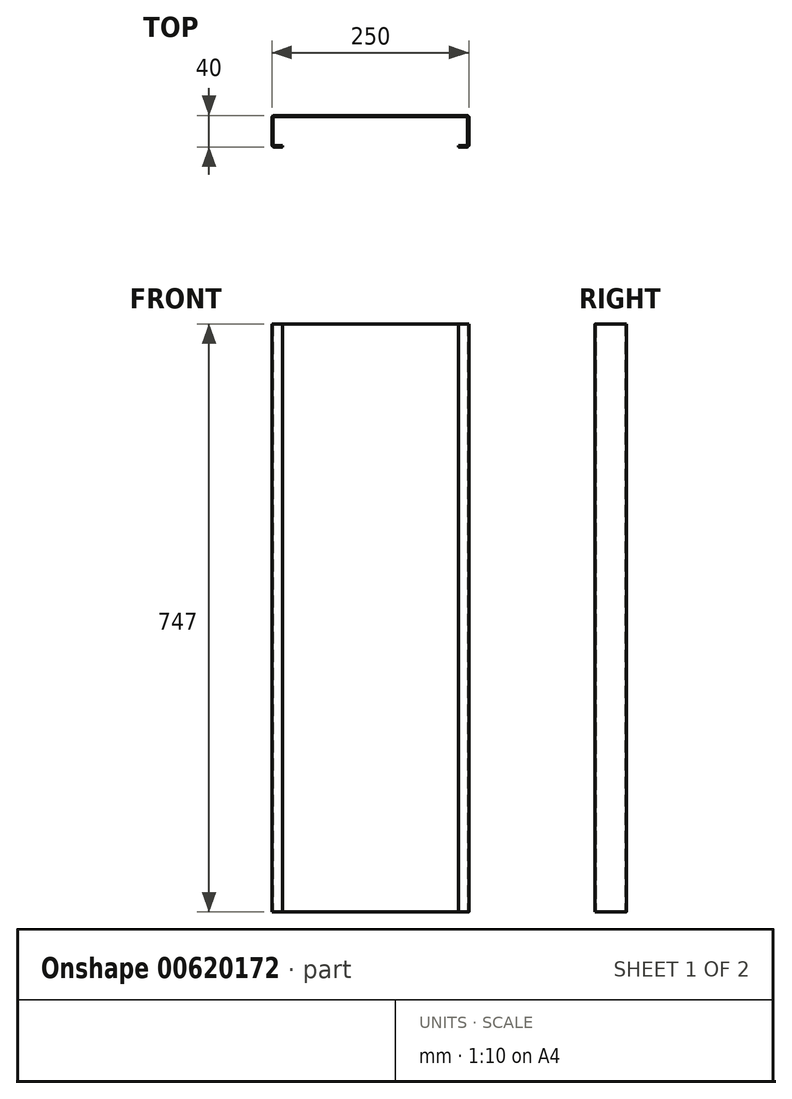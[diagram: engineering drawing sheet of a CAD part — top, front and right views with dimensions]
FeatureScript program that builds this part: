
annotation { "Feature Type Name" : "Feature", "Feature Type Description" : "" }
export const myFeature = defineFeature(function(context is Context, id is Id, definition is map)
    precondition{}
    {
        {
            var Q0;
            Q0=qCreatedBy(makeId("Top.planeOp"),FACE);
            var sketch = newSketch(context, id + "F0", { "sketchPlane" : qUnion([Q0])});
            skLineSegment(sketch, "E0", {"start": v(0, 0) * mm, "end": v(-122.5, 0) * mm});
            skLineSegment(sketch, "E1", {"start": v(-125, -2.5) * mm, "end": v(-125, -37.5) * mm});
            skLineSegment(sketch, "E2", {"start": v(-122.5, -40) * mm, "end": v(-112, -40) * mm});
            skPoint(sketch, "E3.visualSharp", {"position": v(-125, 0) * mm});
            skArc(sketch, "E3.filletArc", {"start": v(-122.5, 0) * mm, "mid": v(-124.27, -0.73) * mm, "end": v(-125, -2.5) * mm});
            skPoint(sketch, "E4.visualSharp", {"position": v(-125, -40) * mm});
            skArc(sketch, "E4.filletArc", {"start": v(-125, -37.5) * mm, "mid": v(-124.27, -39.27) * mm, "end": v(-122.5, -40) * mm});
            skLineSegment(sketch, "E5.0", {"start": v(-122.5, -38.5) * mm, "end": v(-112, -38.5) * mm});
            skLineSegment(sketch, "E5.1", {"start": v(0, -1.5) * mm, "end": v(-122.5, -1.5) * mm});
            skArc(sketch, "E5.2", {"start": v(-122.5, -1.5) * mm, "mid": v(-123.2, -1.8) * mm, "end": v(-123.5, -2.5) * mm});
            skLineSegment(sketch, "E5.3", {"start": v(-123.5, -2.5) * mm, "end": v(-123.5, -37.5) * mm});
            skArc(sketch, "E5.4", {"start": v(-123.5, -37.5) * mm, "mid": v(-123.2, -38.2) * mm, "end": v(-122.5, -38.5) * mm});
            skLineSegment(sketch, "E6", {"start": v(-112, -38.5) * mm, "end": v(-112, -40) * mm});
            skArc(sketch, "E7.MirrorCS", {"start": v(123.5, -37.5) * mm, "mid": v(123.2, -38.2) * mm, "end": v(122.5, -38.5) * mm});
            skLineSegment(sketch, "E8.MirrorCS", {"start": v(112, -38.5) * mm, "end": v(112, -40) * mm});
            skArc(sketch, "E9.MirrorCS", {"start": v(122.5, -1.5) * mm, "mid": v(123.2, -1.8) * mm, "end": v(123.5, -2.5) * mm});
            skArc(sketch, "E10.MirrorCS", {"start": v(125, -37.5) * mm, "mid": v(124.27, -39.27) * mm, "end": v(122.5, -40) * mm});
            skArc(sketch, "E11.MirrorCS", {"start": v(122.5, 0) * mm, "mid": v(124.27, -0.73) * mm, "end": v(125, -2.5) * mm});
            skLineSegment(sketch, "E12.MirrorCS", {"start": v(123.5, -2.5) * mm, "end": v(123.5, -37.5) * mm});
            skPoint(sketch, "E13.MirrorP", {"position": v(125, 0) * mm});
            skLineSegment(sketch, "E14.MirrorCS", {"start": v(0, 0) * mm, "end": v(122.5, 0) * mm});
            skLineSegment(sketch, "E15.MirrorCS", {"start": v(122.5, -40) * mm, "end": v(112, -40) * mm});
            skLineSegment(sketch, "E16.MirrorCS", {"start": v(122.5, -38.5) * mm, "end": v(112, -38.5) * mm});
            skLineSegment(sketch, "E17.MirrorCS", {"start": v(125, -2.5) * mm, "end": v(125, -37.5) * mm});
            skLineSegment(sketch, "E18.MirrorCS", {"start": v(0, -1.5) * mm, "end": v(122.5, -1.5) * mm});
            skPoint(sketch, "E19.MirrorP", {"position": v(125, -40) * mm});
            skSolve(sketch);
        }
        {
            var Q0;
            Q0=makeQuery(id+"F0.imprint","IMPRINT",FACE,{"disambiguationData":[TD([[makeQuery(id+"F0.imprint","IMPRINT",EDGE,{"derivedFrom":sQuery(id+"F0.wireOp",EDGE,"E0")}),1.0]])]});
            extrude(context, id + "F1", {"entities" : qUnion([Q0]), "endBound" : BoundingType.SYMMETRIC, "depth" : 747 * mm, "offsetDistance" : 25 * mm});
        }
        {
            var Q0;
            Q0=makeQuery(id+"F1.opExtrude","CAP_EDGE",EDGE,{"disambiguationData":[OSD([sQuery(id+"F0.wireOp",EDGE,"E6")])],"isStart":true});
            var Q1;
            Q1=makeQuery(id+"F1.opExtrude","CAP_EDGE",EDGE,{"disambiguationData":[OSD([sQuery(id+"F0.wireOp",EDGE,"E8.MirrorCS")])],"isStart":true});
            var Q2;
            Q2=makeQuery(id+"F1.opExtrude","CAP_EDGE",EDGE,{"disambiguationData":[OSD([sQuery(id+"F0.wireOp",EDGE,"E8.MirrorCS")])],"isStart":false});
            var Q3;
            Q3=makeQuery(id+"F1.opExtrude","CAP_EDGE",EDGE,{"disambiguationData":[OSD([sQuery(id+"F0.wireOp",EDGE,"E6")])],"isStart":false});
            fillet(context, id + "F2", {"entities" : qUnion([Q0, Q1, Q2, Q3]), "radius" : 2 * mm, "tangentPropagation" : true, "allowEdgeOverflow" : false});
        }
    });
